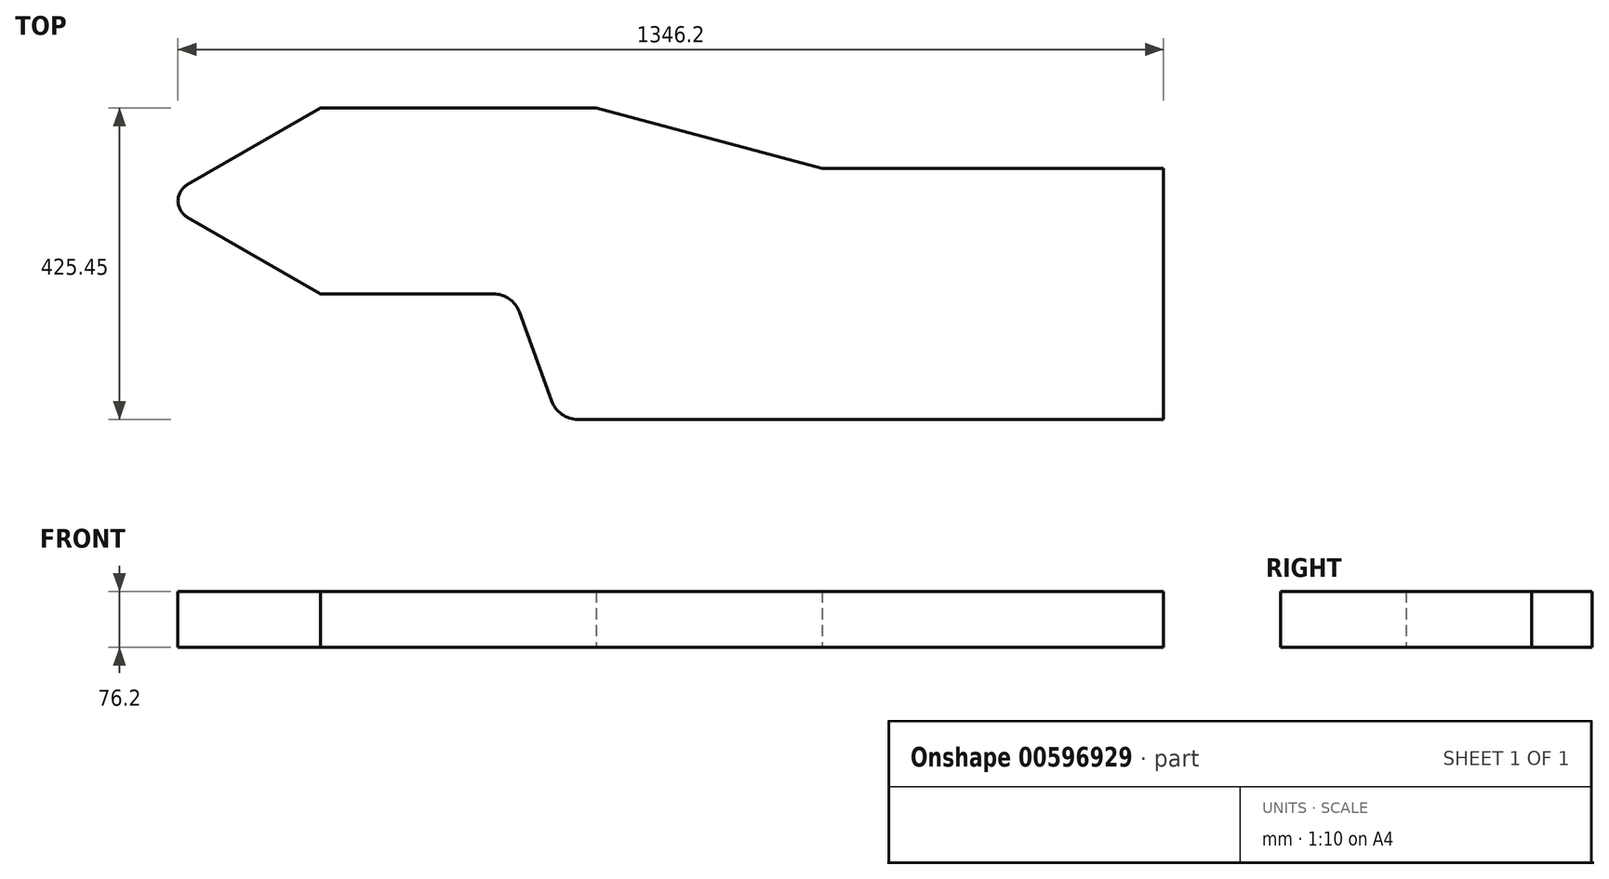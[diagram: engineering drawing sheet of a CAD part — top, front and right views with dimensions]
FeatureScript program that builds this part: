
annotation { "Feature Type Name" : "Feature", "Feature Type Description" : "" }
export const myFeature = defineFeature(function(context is Context, id is Id, definition is map)
    precondition{}
    {
        {
            var Q0;
            Q0=qCreatedBy(makeId("Top.planeOp"),FACE);
            var sketch = newSketch(context, id + "F0", { "sketchPlane" : qUnion([Q0])});
            skLineSegment(sketch, "E0", {"start": v(0, 0) * mm, "end": v(-799.92, 0) * mm});
            skLineSegment(sketch, "E1", {"start": v(-835.72, 25.07) * mm, "end": v(-879.88, 146.38) * mm});
            skLineSegment(sketch, "E2", {"start": v(-915.68, 171.45) * mm, "end": v(-1151.63, 171.45) * mm});
            skLineSegment(sketch, "E3", {"start": v(-1151.63, 171.45) * mm, "end": v(-1333.5, 276.45) * mm});
            skLineSegment(sketch, "E4", {"start": v(-1333.5, 320.45) * mm, "end": v(-1151.63, 425.45) * mm});
            skLineSegment(sketch, "E5", {"start": v(-1151.63, 425.45) * mm, "end": v(-774.7, 425.45) * mm});
            skLineSegment(sketch, "E6", {"start": v(-774.7, 425.45) * mm, "end": v(-466.62, 342.9) * mm});
            skLineSegment(sketch, "E7", {"start": v(-466.62, 342.9) * mm, "end": v(0, 342.9) * mm});
            skLineSegment(sketch, "E8", {"start": v(0, 342.9) * mm, "end": v(0, 0) * mm});
            skPoint(sketch, "E9.visualSharp", {"position": v(-1371.6, 298.45) * mm});
            skArc(sketch, "E9.filletArc", {"start": v(-1333.5, 320.45) * mm, "mid": v(-1346.2, 298.45) * mm, "end": v(-1333.5, 276.45) * mm});
            skPoint(sketch, "E10.visualSharp", {"position": v(-889, 171.45) * mm});
            skArc(sketch, "E10.filletArc", {"start": v(-879.88, 146.38) * mm, "mid": v(-893.82, 164.56) * mm, "end": v(-915.68, 171.45) * mm});
            skPoint(sketch, "E11.visualSharp", {"position": v(-826.6, 0) * mm});
            skArc(sketch, "E11.filletArc", {"start": v(-835.72, 25.07) * mm, "mid": v(-821.77, 6.9) * mm, "end": v(-799.92, 0) * mm});
            skSolve(sketch);
        }
        {
            var Q0;
            Q0 = qSketchRegion(id + "F0", true);
            extrude(context, id + "F1", {"entities" : qUnion([Q0]), "depth" : 76.2 * mm, "offsetDistance" : 25.4 * mm});
        }
    });
